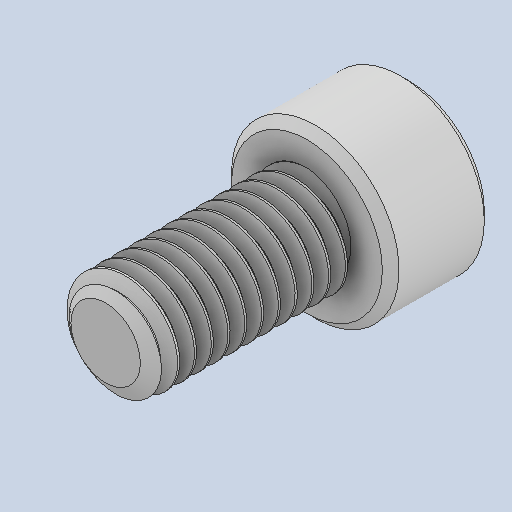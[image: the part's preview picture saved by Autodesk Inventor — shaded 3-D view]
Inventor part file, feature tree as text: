
AUTODESK INVENTOR PART (.ipt)
format: ipt  version: 2023 (Build 270158030, 158C)  size: 528,896 bytes
history: native  units: in
note: dims shown in document units (in); Inventor stores cm internally (conversion verified against a paired STEP export)
features: chamfer x1
ambient origin geometry x8: Origin, YZ Plane, XZ Plane, XY Plane, X Axis, Y Axis, Z Axis, Center Point
bodies: Solid1 (feature_tree)
feature tree (1):
  chamfer  "Chamfer1"  [1 undecoded]
note: 1 required parameter value undecoded (feature->parameter linkage not recoverable at this tier; creation-order binding heuristic only, values carry confidence <= 0.55)
